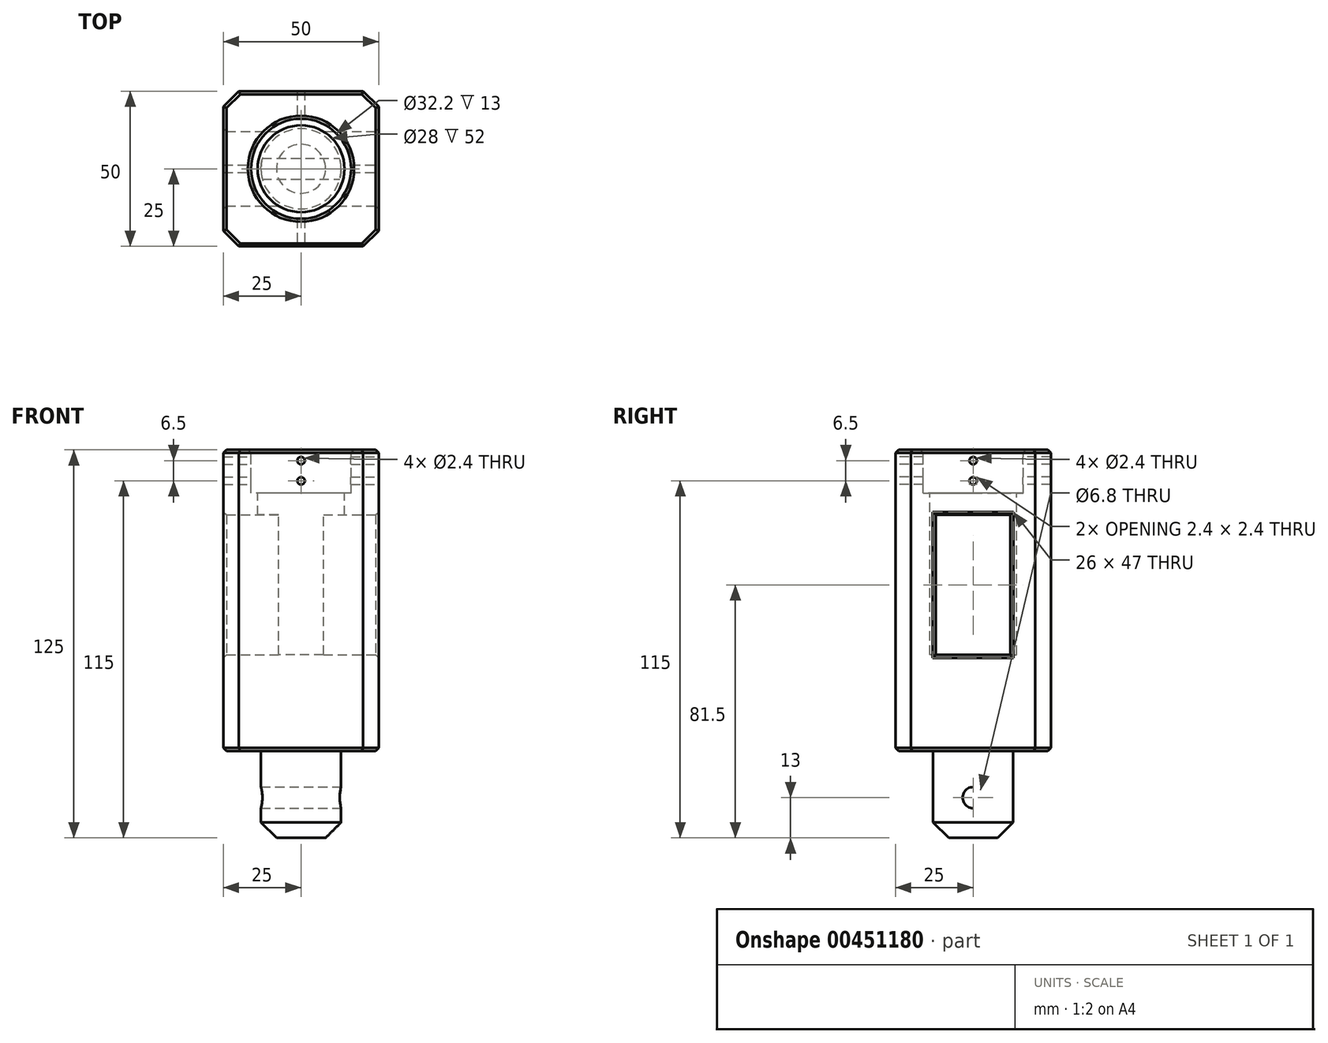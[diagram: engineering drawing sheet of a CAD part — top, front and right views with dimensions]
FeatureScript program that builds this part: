
annotation { "Feature Type Name" : "Feature", "Feature Type Description" : "" }
export const myFeature = defineFeature(function(context is Context, id is Id, definition is map)
    precondition{}
    {
        {
            var Q0;
            Q0=qCreatedBy(makeId("Top.planeOp"),FACE);
            var sketch = newSketch(context, id + "F0", { "sketchPlane" : qUnion([Q0])});
            skCircle(sketch, "E0", {"center": v(0, 0) * mm, "radius": 12.9 * mm});
            skSolve(sketch);
        }
        {
            var Q0;
            Q0=qSketchRegion(id+"F0",true);
            extrude(context, id + "F1", {"entities" : qUnion([Q0]), "depth" : 28 * mm, "offsetDistance" : 25 * mm});
        }
        {
            var Q0;
            Q0=makeQuery(id+"F1.opExtrude","CAP_FACE",FACE,{"disambiguationData":[OSD([sQuery(id+"F0.wireOp",EDGE,"E0"),sQuery(id+"F0.wireOp",EDGE,"SnAVlE3f-jAuu-pCCq-HaNH-xM0daaBw2DbN")])],"isStart":false});
            var sketch = newSketch(context, id + "F2", { "sketchPlane" : qUnion([Q0])});
            skCircle(sketch, "E1", {"center": v(0, 0) * mm, "radius": 19 * mm, "construction": true});
            skLineSegment(sketch, "E2.bottom", {"start": v(25, -25) * mm, "end": v(-25, -25) * mm});
            skLineSegment(sketch, "E2.top", {"start": v(25, 25) * mm, "end": v(-25, 25) * mm});
            skLineSegment(sketch, "E2.left", {"start": v(25, -25) * mm, "end": v(25, 25) * mm});
            skLineSegment(sketch, "E2.right", {"start": v(-25, -25) * mm, "end": v(-25, 25) * mm});
            skSolve(sketch);
        }
        {
            var Q0;
            Q0=qSketchRegion(id+"F2",true);
            extrude(context, id + "F3", {"entities" : qUnion([Q0]), "operationType" : NewBodyOperationType.ADD, "depth" : 97 * mm, "offsetDistance" : 25 * mm});
        }
        {
            var Q0;
            Q0=makeQuery(id+"F3.opExtrude","CAP_FACE",FACE,{"disambiguationData":[OSD([sQuery(id+"F2.wireOp",EDGE,"E2.bottom"),sQuery(id+"F2.wireOp",EDGE,"E2.top"),sQuery(id+"F2.wireOp",EDGE,"E2.left"),sQuery(id+"F2.wireOp",EDGE,"E2.right")])],"isStart":false});
            var sketch = newSketch(context, id + "F4", { "sketchPlane" : qUnion([Q0])});
            skCircle(sketch, "E3", {"center": v(0, 0) * mm, "radius": 14 * mm});
            skSolve(sketch);
        }
        {
            var Q0;
            Q0=qSketchRegion(id+"F4",true);
            extrude(context, id + "F5", {"entities" : qUnion([Q0]), "operationType" : NewBodyOperationType.REMOVE, "oppositeDirection" : true, "depth" : 66 * mm, "offsetDistance" : 25 * mm});
        }
        {
            var Q0;
            Q0=makeQuery(id+"F3.opExtrude","CAP_FACE",FACE,{"disambiguationData":[OSD([sQuery(id+"F2.wireOp",EDGE,"E2.bottom"),sQuery(id+"F2.wireOp",EDGE,"E2.top"),sQuery(id+"F2.wireOp",EDGE,"E2.left"),sQuery(id+"F2.wireOp",EDGE,"E2.right")])],"isStart":false});
            var sketch = newSketch(context, id + "F6", { "sketchPlane" : qUnion([Q0])});
            skCircle(sketch, "E4", {"center": v(0, 0) * mm, "radius": 16.1 * mm});
            skSolve(sketch);
        }
        {
            var Q0;
            Q0=qSketchRegion(id+"F6",true);
            extrude(context, id + "F7", {"entities" : qUnion([Q0]), "operationType" : NewBodyOperationType.REMOVE, "oppositeDirection" : true, "depth" : 14 * mm, "offsetDistance" : 25 * mm});
        }
        {
            var Q0;
            Q0=qCreatedBy(makeId("Right.planeOp"),FACE);
            var sketch = newSketch(context, id + "F8", { "sketchPlane" : qUnion([Q0])});
            skCircle(sketch, "E5", {"center": v(0, 13) * mm, "radius": 3.4 * mm});
            skSolve(sketch);
        }
        {
            var Q0;
            Q0=qSketchRegion(id+"F8",true);
            extrude(context, id + "F9", {"entities" : qUnion([Q0]), "operationType" : NewBodyOperationType.REMOVE, "oppositeDirection" : true, "depth" : 30 * mm, "offsetDistance" : 25 * mm, "symmetric" : true});
        }
        {
            var Q0;
            Q0=qCreatedBy(makeId("Front.planeOp"),FACE);
            var sketch = newSketch(context, id + "F10", { "sketchPlane" : qUnion([Q0])});
            skCircle(sketch, "E6", {"center": v(0, 121.5) * mm, "radius": 1.2 * mm});
            skCircle(sketch, "E7", {"center": v(0, 115) * mm, "radius": 1.2 * mm});
            skSolve(sketch);
        }
        {
            var Q0;
            Q0=qSketchRegion(id+"F10",true);
            extrude(context, id + "F11", {"entities" : qUnion([Q0]), "operationType" : NewBodyOperationType.REMOVE, "oppositeDirection" : true, "depth" : 102.8 * mm, "offsetDistance" : 25 * mm, "symmetric" : true});
        }
        {
            var Q0;
            Q0=qCreatedBy(makeId("Right.planeOp"),FACE);
            var sketch = newSketch(context, id + "F12", { "sketchPlane" : qUnion([Q0])});
            skCircle(sketch, "E8", {"center": v(0, 121.5) * mm, "radius": 1.2 * mm});
            skCircle(sketch, "E9", {"center": v(0, 115) * mm, "radius": 1.2 * mm});
            skLineSegment(sketch, "E10.bottom", {"start": v(12, 59) * mm, "end": v(-12, 59) * mm});
            skLineSegment(sketch, "E10.top", {"start": v(12, 104) * mm, "end": v(-12, 104) * mm});
            skLineSegment(sketch, "E10.left", {"start": v(12, 59) * mm, "end": v(12, 104) * mm});
            skLineSegment(sketch, "E10.right", {"start": v(-12, 59) * mm, "end": v(-12, 104) * mm});
            skPoint(sketch, "E10.middle", {"position": v(0, 81.5) * mm});
            skSolve(sketch);
        }
        {
            var Q0;
            Q0=qSketchRegion(id+"F12",true);
            extrude(context, id + "F13", {"entities" : qUnion([Q0]), "operationType" : NewBodyOperationType.REMOVE, "oppositeDirection" : true, "depth" : 75.6 * mm, "offsetDistance" : 25 * mm, "symmetric" : true});
        }
        {
            var Q0;
            Q0=makeQuery(id+"F1.opExtrude","CAP_EDGE",EDGE,{"disambiguationData":[OSD([sQuery(id+"F0.wireOp",EDGE,"E0")])],"isStart":true});
            var Q1;
            Q1=makeQuery(id+"F3.opExtrude","SWEPT_EDGE",EDGE,{"disambiguationData":[OSD([sQuery(id+"F2.wireOp",EDGE,"E2.top"),sQuery(id+"F2.wireOp",EDGE,"E2.right")])]});
            var Q2;
            Q2=makeQuery(id+"F3.opExtrude","SWEPT_EDGE",EDGE,{"disambiguationData":[OSD([sQuery(id+"F2.wireOp",EDGE,"E2.bottom"),sQuery(id+"F2.wireOp",EDGE,"E2.right")])]});
            var Q3;
            Q3=makeQuery(id+"F3.opExtrude","SWEPT_EDGE",EDGE,{"disambiguationData":[OSD([sQuery(id+"F2.wireOp",EDGE,"E2.bottom"),sQuery(id+"F2.wireOp",EDGE,"E2.left")])]});
            var Q4;
            Q4=makeQuery(id+"F3.opExtrude","SWEPT_EDGE",EDGE,{"disambiguationData":[OSD([sQuery(id+"F2.wireOp",EDGE,"E2.top"),sQuery(id+"F2.wireOp",EDGE,"E2.left")])]});
            chamfer(context, id + "F14", {"entities" : qUnion([Q0, Q1, Q2, Q3, Q4]), "width" : 5 * mm, "tangentPropagation" : true});
        }
        {
            var Q0;
            Q0=makeQuery(id+"F7.boolean.opBoolean","COPY",EDGE,{"derivedFrom":makeQuery(id+"F7.opExtrude","CAP_EDGE",EDGE,{"disambiguationData":[OSD([sQuery(id+"F6.wireOp",EDGE,"E4")])],"isStart":true})});
            var Q1;
            Q1=makeQuery(id+"F3.opExtrude","CAP_FACE",FACE,{"disambiguationData":[OSD([sQuery(id+"F2.wireOp",EDGE,"E2.bottom"),sQuery(id+"F2.wireOp",EDGE,"E2.top"),sQuery(id+"F2.wireOp",EDGE,"E2.left"),sQuery(id+"F2.wireOp",EDGE,"E2.right")])],"isStart":false});
            var Q2;
            Q2=makeQuery(id+"F3.opExtrude","CAP_EDGE",EDGE,{"disambiguationData":[OSD([sQuery(id+"F2.wireOp",EDGE,"E2.right")])],"isStart":true});
            var Q3;
            Q3=makeQuery(id+"F3.opExtrude","CAP_EDGE",EDGE,{"disambiguationData":[OSD([sQuery(id+"F2.wireOp",EDGE,"E2.top")])],"isStart":true});
            var Q4;
            {var subQ0=sQuery(id+"F2.wireOp",EDGE,"E2.right");var subQ1=sQuery(id+"F2.wireOp",EDGE,"E2.top");Q4=makeQuery(id+"F14.opChamfer","BLEND_EDGE",EDGE,{"blendedFrom":[makeQuery(id+"F3.opExtrude","SWEPT_EDGE",EDGE,{"disambiguationData":[OSD([subQ1,subQ0])]}),makeQuery(id+"F3.opExtrude","CAP_FACE",FACE,{"disambiguationData":[OSD([sQuery(id+"F2.wireOp",EDGE,"E2.bottom"),subQ1,sQuery(id+"F2.wireOp",EDGE,"E2.left"),subQ0])],"isStart":true})],"blendedInto":[makeQuery(id+"F3.opExtrude","CAP_FACE",FACE,{"disambiguationData":[OSD([sQuery(id+"F2.wireOp",EDGE,"E2.bottom"),subQ1,sQuery(id+"F2.wireOp",EDGE,"E2.left"),subQ0])],"isStart":true})]});}
            var Q5;
            Q5=makeQuery(id+"F3.opExtrude","CAP_EDGE",EDGE,{"disambiguationData":[OSD([sQuery(id+"F2.wireOp",EDGE,"E2.bottom")])],"isStart":true});
            var Q6;
            {var subQ0=sQuery(id+"F2.wireOp",EDGE,"E2.right");var subQ1=sQuery(id+"F2.wireOp",EDGE,"E2.bottom");Q6=makeQuery(id+"F14.opChamfer","BLEND_EDGE",EDGE,{"blendedFrom":[makeQuery(id+"F3.opExtrude","SWEPT_EDGE",EDGE,{"disambiguationData":[OSD([subQ1,subQ0])]}),makeQuery(id+"F3.opExtrude","CAP_FACE",FACE,{"disambiguationData":[OSD([subQ1,sQuery(id+"F2.wireOp",EDGE,"E2.top"),sQuery(id+"F2.wireOp",EDGE,"E2.left"),subQ0])],"isStart":true})],"blendedInto":[makeQuery(id+"F3.opExtrude","CAP_FACE",FACE,{"disambiguationData":[OSD([subQ1,sQuery(id+"F2.wireOp",EDGE,"E2.top"),sQuery(id+"F2.wireOp",EDGE,"E2.left"),subQ0])],"isStart":true})]});}
            var Q7;
            {var subQ0=sQuery(id+"F2.wireOp",EDGE,"E2.left");var subQ1=sQuery(id+"F2.wireOp",EDGE,"E2.bottom");Q7=makeQuery(id+"F14.opChamfer","BLEND_EDGE",EDGE,{"blendedFrom":[makeQuery(id+"F3.opExtrude","SWEPT_EDGE",EDGE,{"disambiguationData":[OSD([subQ1,subQ0])]}),makeQuery(id+"F3.opExtrude","CAP_FACE",FACE,{"disambiguationData":[OSD([subQ1,sQuery(id+"F2.wireOp",EDGE,"E2.top"),subQ0,sQuery(id+"F2.wireOp",EDGE,"E2.right")])],"isStart":true})],"blendedInto":[makeQuery(id+"F3.opExtrude","CAP_FACE",FACE,{"disambiguationData":[OSD([subQ1,sQuery(id+"F2.wireOp",EDGE,"E2.top"),subQ0,sQuery(id+"F2.wireOp",EDGE,"E2.right")])],"isStart":true})]});}
            var Q8;
            Q8=makeQuery(id+"F3.opExtrude","CAP_EDGE",EDGE,{"disambiguationData":[OSD([sQuery(id+"F2.wireOp",EDGE,"E2.left")])],"isStart":true});
            var Q9;
            {var subQ0=sQuery(id+"F2.wireOp",EDGE,"E2.left");var subQ1=sQuery(id+"F2.wireOp",EDGE,"E2.top");Q9=makeQuery(id+"F14.opChamfer","BLEND_EDGE",EDGE,{"blendedFrom":[makeQuery(id+"F3.opExtrude","SWEPT_EDGE",EDGE,{"disambiguationData":[OSD([subQ1,subQ0])]}),makeQuery(id+"F3.opExtrude","CAP_FACE",FACE,{"disambiguationData":[OSD([sQuery(id+"F2.wireOp",EDGE,"E2.bottom"),subQ1,subQ0,sQuery(id+"F2.wireOp",EDGE,"E2.right")])],"isStart":true})],"blendedInto":[makeQuery(id+"F3.opExtrude","CAP_FACE",FACE,{"disambiguationData":[OSD([sQuery(id+"F2.wireOp",EDGE,"E2.bottom"),subQ1,subQ0,sQuery(id+"F2.wireOp",EDGE,"E2.right")])],"isStart":true})]});}
            var Q10;
            Q10=makeQuery(id+"F13.boolean.opBoolean","INTERSECT",EDGE,{"derivedFrom":[makeQuery(id+"F3.opExtrude","SWEPT_FACE",FACE,{"disambiguationData":[OSD([sQuery(id+"F2.wireOp",EDGE,"E2.right")])]}),makeQuery(id+"F13.opExtrude","SWEPT_FACE",FACE,{"disambiguationData":[OSD([sQuery(id+"F12.wireOp",EDGE,"E10.bottom")])]})]});
            var Q11;
            Q11=makeQuery(id+"F13.boolean.opBoolean","INTERSECT",EDGE,{"derivedFrom":[makeQuery(id+"F3.opExtrude","SWEPT_FACE",FACE,{"disambiguationData":[OSD([sQuery(id+"F2.wireOp",EDGE,"E2.right")])]}),makeQuery(id+"F13.opExtrude","SWEPT_FACE",FACE,{"disambiguationData":[OSD([sQuery(id+"F12.wireOp",EDGE,"E10.left")])]})]});
            var Q12;
            Q12=makeQuery(id+"F13.boolean.opBoolean","INTERSECT",EDGE,{"derivedFrom":[makeQuery(id+"F3.opExtrude","SWEPT_FACE",FACE,{"disambiguationData":[OSD([sQuery(id+"F2.wireOp",EDGE,"E2.right")])]}),makeQuery(id+"F13.opExtrude","SWEPT_FACE",FACE,{"disambiguationData":[OSD([sQuery(id+"F12.wireOp",EDGE,"E10.top")])]})]});
            var Q13;
            Q13=makeQuery(id+"F13.boolean.opBoolean","INTERSECT",EDGE,{"derivedFrom":[makeQuery(id+"F3.opExtrude","SWEPT_FACE",FACE,{"disambiguationData":[OSD([sQuery(id+"F2.wireOp",EDGE,"E2.right")])]}),makeQuery(id+"F13.opExtrude","SWEPT_FACE",FACE,{"disambiguationData":[OSD([sQuery(id+"F12.wireOp",EDGE,"E10.right")])]})]});
            var Q14;
            Q14=makeQuery(id+"F13.boolean.opBoolean","INTERSECT",EDGE,{"derivedFrom":[makeQuery(id+"F3.opExtrude","SWEPT_FACE",FACE,{"disambiguationData":[OSD([sQuery(id+"F2.wireOp",EDGE,"E2.left")])]}),makeQuery(id+"F13.opExtrude","SWEPT_FACE",FACE,{"disambiguationData":[OSD([sQuery(id+"F12.wireOp",EDGE,"E10.bottom")])]})]});
            var Q15;
            Q15=makeQuery(id+"F13.boolean.opBoolean","INTERSECT",EDGE,{"derivedFrom":[makeQuery(id+"F3.opExtrude","SWEPT_FACE",FACE,{"disambiguationData":[OSD([sQuery(id+"F2.wireOp",EDGE,"E2.left")])]}),makeQuery(id+"F13.opExtrude","SWEPT_FACE",FACE,{"disambiguationData":[OSD([sQuery(id+"F12.wireOp",EDGE,"E10.right")])]})]});
            var Q16;
            Q16=makeQuery(id+"F13.boolean.opBoolean","INTERSECT",EDGE,{"derivedFrom":[makeQuery(id+"F3.opExtrude","SWEPT_FACE",FACE,{"disambiguationData":[OSD([sQuery(id+"F2.wireOp",EDGE,"E2.left")])]}),makeQuery(id+"F13.opExtrude","SWEPT_FACE",FACE,{"disambiguationData":[OSD([sQuery(id+"F12.wireOp",EDGE,"E10.left")])]})]});
            var Q17;
            Q17=makeQuery(id+"F13.boolean.opBoolean","INTERSECT",EDGE,{"derivedFrom":[makeQuery(id+"F3.opExtrude","SWEPT_FACE",FACE,{"disambiguationData":[OSD([sQuery(id+"F2.wireOp",EDGE,"E2.left")])]}),makeQuery(id+"F13.opExtrude","SWEPT_FACE",FACE,{"disambiguationData":[OSD([sQuery(id+"F12.wireOp",EDGE,"E10.top")])]})]});
            chamfer(context, id + "F15", {"entities" : qUnion([Q0, Q1, Q2, Q3, Q4, Q5, Q6, Q7, Q8, Q9, Q10, Q11, Q12, Q13, Q14, Q15, Q16, Q17]), "width" : 1 * mm, "tangentPropagation" : true});
        }
    });
